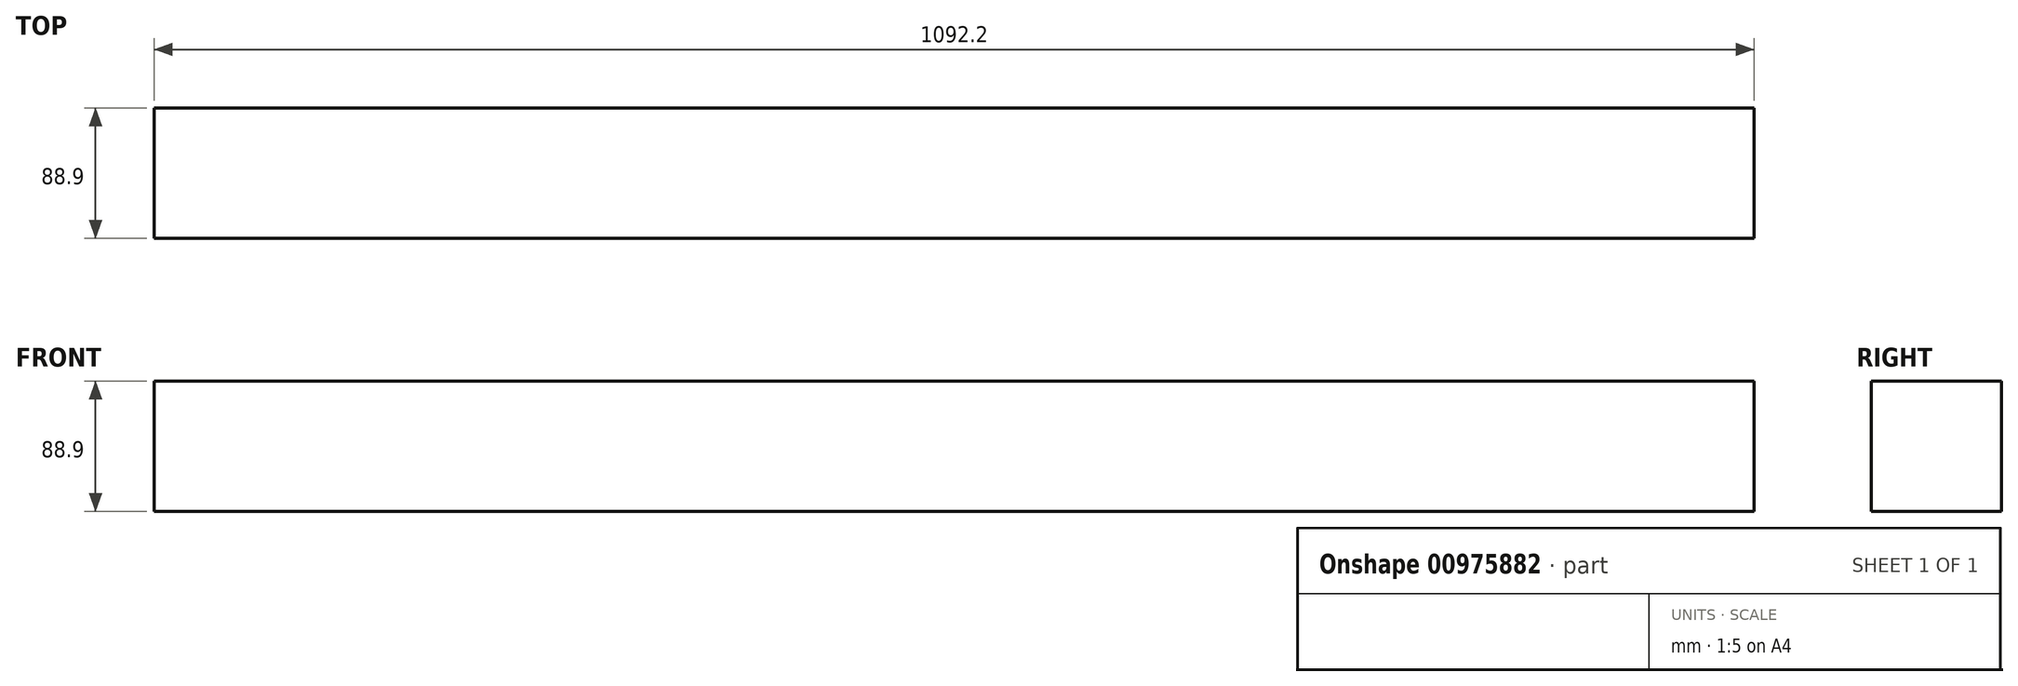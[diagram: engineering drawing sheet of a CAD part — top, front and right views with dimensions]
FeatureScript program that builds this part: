
annotation { "Feature Type Name" : "Feature", "Feature Type Description" : "" }
export const myFeature = defineFeature(function(context is Context, id is Id, definition is map)
    precondition{}
    {
        {
            var Q0;
            Q0=qCreatedBy(makeId("Right.planeOp"),FACE);
            var sketch = newSketch(context, id + "F0", { "sketchPlane" : qUnion([Q0])});
            skLineSegment(sketch, "E0.bottom", {"start": v(0, 0) * mm, "end": v(0, 0) * mm});
            skLineSegment(sketch, "E0.top", {"start": v(0, 0) * mm, "end": v(0, 0) * mm});
            skLineSegment(sketch, "E0.left", {"start": v(0, 0) * mm, "end": v(0, 0) * mm});
            skLineSegment(sketch, "E0.right", {"start": v(0, 0) * mm, "end": v(0, 0) * mm});
            skPoint(sketch, "E0.middle", {"position": v(0, 0) * mm});
            skLineSegment(sketch, "E1.bottom", {"start": v(44.45, 44.45) * mm, "end": v(-44.45, 44.45) * mm});
            skLineSegment(sketch, "E1.top", {"start": v(44.45, -44.45) * mm, "end": v(-44.45, -44.45) * mm});
            skLineSegment(sketch, "E1.left", {"start": v(44.45, 44.45) * mm, "end": v(44.45, -44.45) * mm});
            skLineSegment(sketch, "E1.right", {"start": v(-44.45, 44.45) * mm, "end": v(-44.45, -44.45) * mm});
            skSolve(sketch);
        }
        {
            var Q0;
            Q0=qSketchRegion(id+"F0",true);
            extrude(context, id + "F1", {"entities" : qUnion([Q0]), "depth" : 1092.2 * mm, "offsetDistance" : 25.4 * mm});
        }
    });
